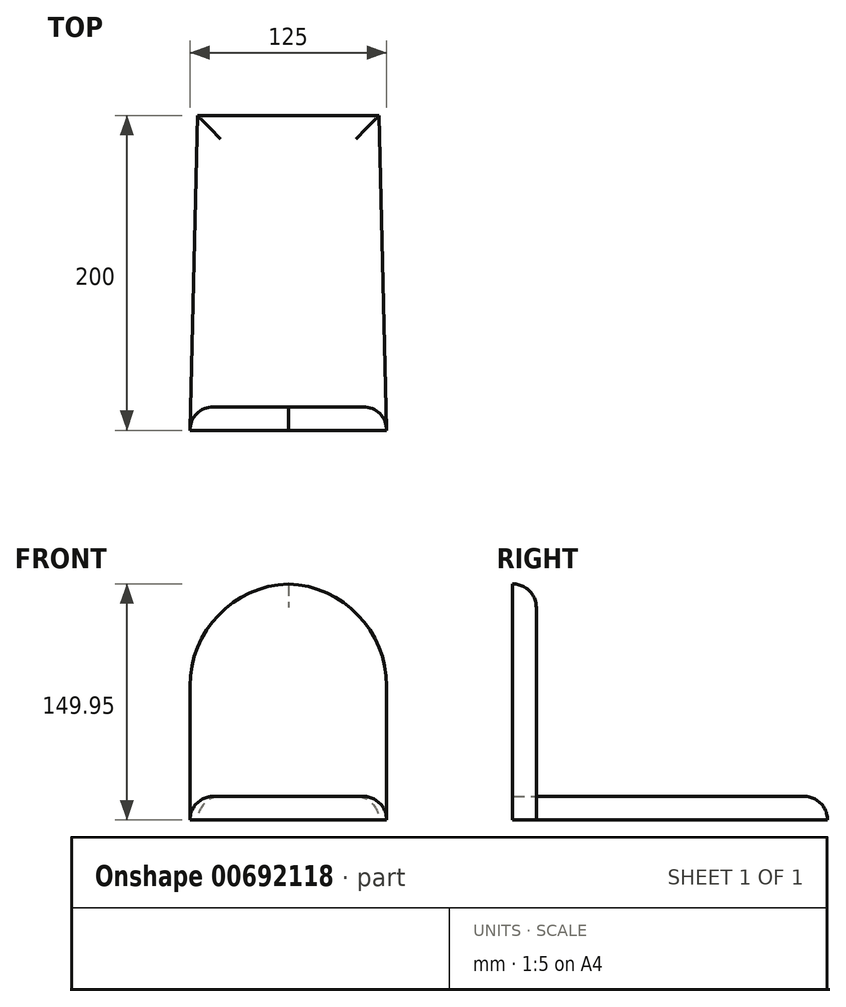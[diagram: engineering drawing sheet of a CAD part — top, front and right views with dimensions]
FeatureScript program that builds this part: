
annotation { "Feature Type Name" : "Feature", "Feature Type Description" : "" }
export const myFeature = defineFeature(function(context is Context, id is Id, definition is map)
    precondition{}
    {
        {
            var Q0;
            Q0=qCreatedBy(makeId("Front.planeOp"),FACE);
            var sketch = newSketch(context, id + "F0", { "sketchPlane" : qUnion([Q0])});
            skLineSegment(sketch, "E0.bottom", {"start": v(62.5, -75) * mm, "end": v(-62.5, -75) * mm});
            skLineSegment(sketch, "E0.top", {"start": v(2.5, 75) * mm, "end": v(-2.5, 75) * mm});
            skLineSegment(sketch, "E0.left", {"start": v(62.5, -75) * mm, "end": v(62.5, 10) * mm});
            skLineSegment(sketch, "E0.right", {"start": v(-62.5, -75) * mm, "end": v(-62.5, 10) * mm});
            skPoint(sketch, "E0.middle", {"position": v(0, 0) * mm});
            skPoint(sketch, "E1.visualSharp", {"position": v(-62.5, 75) * mm});
            skArc(sketch, "E1.filletArc", {"start": v(2.5, 75) * mm, "mid": v(-43.46, 55.96) * mm, "end": v(-62.5, 10) * mm});
            skPoint(sketch, "E2.visualSharp", {"position": v(62.5, 75) * mm});
            skArc(sketch, "E2.filletArc", {"start": v(62.5, 10) * mm, "mid": v(43.46, 55.96) * mm, "end": v(-2.5, 75) * mm});
            skSolve(sketch);
        }
        {
            var Q0;
            Q0=sQuery(id+"F0.wireOp",EDGE,"E0.bottom");
            cPlane(context, id + "F1", {"entities" : qUnion([Q0]), "cplaneType" : CPlaneType.LINE_ANGLE, "offset" : 25 * mm, "angle" : 270 * degree, "width" : 150 * mm, "height" : 150 * mm});
        }
        {
            var Q0;
            Q0=qCreatedBy(id+"F1.planeOp",FACE);
            var sketch = newSketch(context, id + "F2", { "sketchPlane" : qUnion([Q0])});
            skPoint(sketch, "E3.0", {"position": v(-62.5, 0) * mm});
            skLineSegment(sketch, "E4", {"start": v(57.5, -200) * mm, "end": v(-57.5, -200) * mm});
            skLineSegment(sketch, "E5", {"start": v(62.5, 0) * mm, "end": v(-62.5, 0) * mm});
            skLineSegment(sketch, "E6", {"start": v(-62.5, 0) * mm, "end": v(-57.5, -200) * mm});
            skLineSegment(sketch, "E7", {"start": v(62.5, 0) * mm, "end": v(57.5, -200) * mm});
            skSolve(sketch);
        }
        {
            var Q0;
            Q0=makeQuery(id+"F2.imprint","IMPRINT",FACE,{"disambiguationData":[TD([[makeQuery(id+"F2.imprint","IMPRINT",EDGE,{"derivedFrom":sQuery(id+"F2.wireOp",EDGE,"E4")}),-1.0]])]});
            extrude(context, id + "F3", {"entities" : qUnion([Q0]), "oppositeDirection" : true, "depth" : 15 * mm, "offsetDistance" : 25 * mm});
        }
        {
            var Q0;
            Q0=makeQuery(id+"F0.imprint","IMPRINT",FACE,{"disambiguationData":[TD([[makeQuery(id+"F0.imprint","IMPRINT",EDGE,{"derivedFrom":sQuery(id+"F0.wireOp",EDGE,"E0.bottom")}),-1.0]])]});
            extrude(context, id + "F4", {"entities" : qUnion([Q0]), "oppositeDirection" : true, "depth" : 15 * mm, "offsetDistance" : 25 * mm});
        }
        {
            var Q0;
            Q0=makeQuery(id+"F4.opExtrude","CAP_EDGE",EDGE,{"disambiguationData":[OSD([sQuery(id+"F0.wireOp",EDGE,"E2.filletArc")])],"isStart":false});
            var Q1;
            Q1=makeQuery(id+"F4.opExtrude","CAP_EDGE",EDGE,{"disambiguationData":[OSD([sQuery(id+"F0.wireOp",EDGE,"E0.right")])],"isStart":false});
            fillet(context, id + "F5", {"entities" : qUnion([Q0, Q1]), "radius" : 15 * mm, "tangentPropagation" : true, "allowEdgeOverflow" : false});
        }
        {
            var Q0;
            Q0=makeQuery(id+"F3.opExtrude","CAP_EDGE",EDGE,{"disambiguationData":[OSD([sQuery(id+"F2.wireOp",EDGE,"E4")])],"isStart":false});
            var Q1;
            {var subQ1=sQuery(id+"F2.wireOp",EDGE,"E4");var subQ2=sQuery(id+"F2.wireOp",EDGE,"oBLzPGlP-Jrb6-vdDq-hUp4-seYBUfKwnkqt");Q1=makeQuery(id+"F4.boolean.opBoolean","SPLIT",EDGE,{"disambiguationData":[TD([makeQuery(id+"F3.opExtrude","SWEPT_FACE",FACE,{"disambiguationData":[OSD([subQ1])]})])],"derivedFrom":makeQuery(id+"F3.opExtrude","CAP_EDGE",EDGE,{"disambiguationData":[OSD([subQ2])],"isStart":false})});}
            var Q2;
            {var subQ0=sQuery(id+"F2.wireOp",EDGE,"E4");var subQ2=sQuery(id+"F2.wireOp",EDGE,"f92abb86-c033-4437-a907-b808812c1666.0");Q2=makeQuery(id+"F4.boolean.opBoolean","SPLIT",EDGE,{"disambiguationData":[TD([makeQuery(id+"F3.opExtrude","SWEPT_FACE",FACE,{"disambiguationData":[OSD([subQ0])]})])],"derivedFrom":makeQuery(id+"F3.opExtrude","CAP_EDGE",EDGE,{"disambiguationData":[OSD([subQ2])],"isStart":false})});}
            var Q3;
            Q3=makeQuery(id+"F3.opExtrude","CAP_EDGE",EDGE,{"disambiguationData":[OSD([sQuery(id+"F2.wireOp",EDGE,"E7")])],"isStart":false});
            var Q4;
            Q4=makeQuery(id+"F3.opExtrude","CAP_EDGE",EDGE,{"disambiguationData":[OSD([sQuery(id+"F2.wireOp",EDGE,"E6")])],"isStart":false});
            fillet(context, id + "F6", {"entities" : qUnion([Q0, Q1, Q2, Q3, Q4]), "radius" : 15 * mm, "tangentPropagation" : true, "allowEdgeOverflow" : false});
        }
    });
